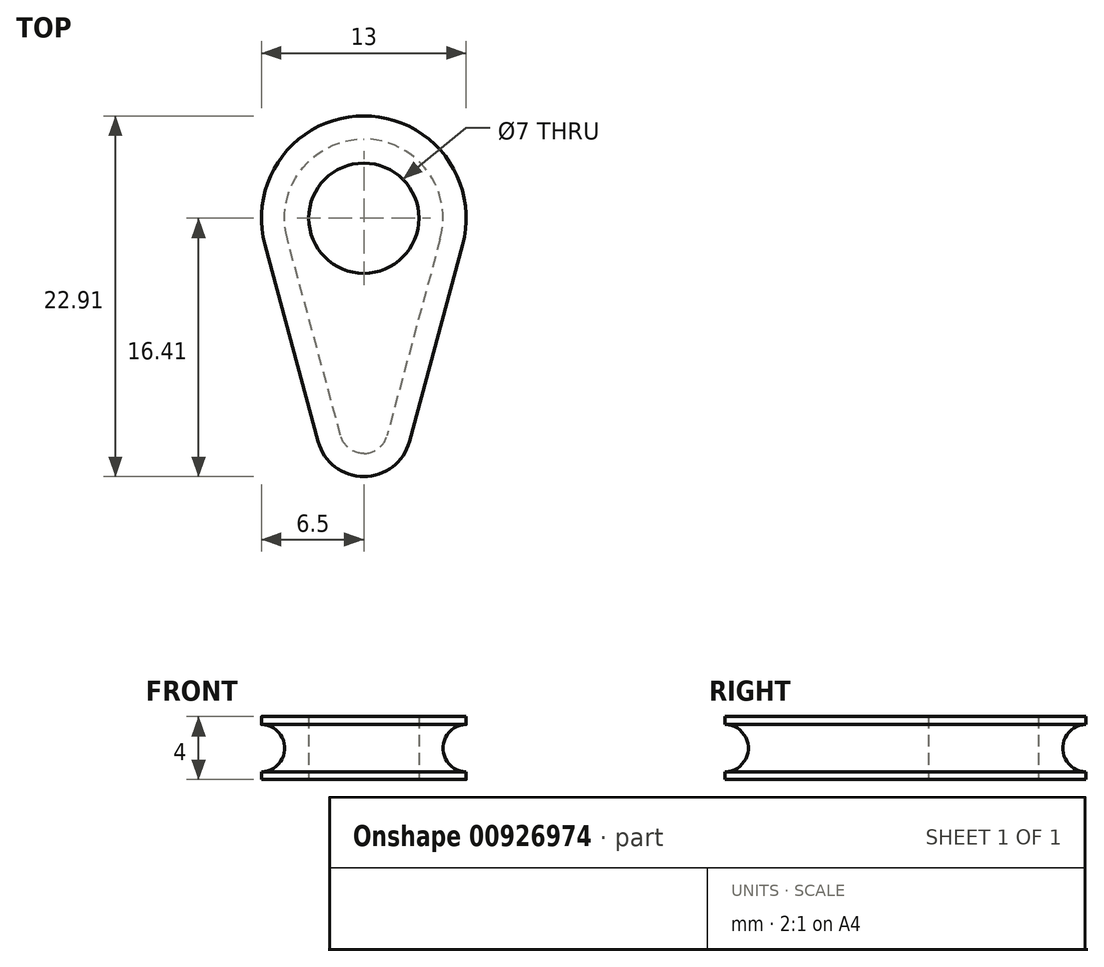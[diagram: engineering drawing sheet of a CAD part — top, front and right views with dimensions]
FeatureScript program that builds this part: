
annotation { "Feature Type Name" : "Feature", "Feature Type Description" : "" }
export const myFeature = defineFeature(function(context is Context, id is Id, definition is map)
    precondition{}
    {
        {
            var Q0;
            Q0=qCreatedBy(makeId("Top.planeOp"),FACE);
            var sketch = newSketch(context, id + "F0", { "sketchPlane" : qUnion([Q0])});
            skLineSegment(sketch, "E0", {"start": v(0, 71.12) * mm, "end": v(0, 6.5) * mm});
            skArc(sketch, "E1", {"start": v(0, 3.5) * mm, "mid": v(-3.5, 0) * mm, "end": v(0, -3.5) * mm});
            skArc(sketch, "E2", {"start": v(0, 6.5) * mm, "mid": v(-5.16, 3.95) * mm, "end": v(-6.27, -1.7) * mm});
            skLineSegment(sketch, "E3", {"start": v(0, 6.5) * mm, "end": v(0, -16.42) * mm});
            skArc(sketch, "E4", {"start": v(-2.9, -14.2) * mm, "mid": v(-1.82, -15.8) * mm, "end": v(0, -16.41) * mm});
            skLineSegment(sketch, "E5", {"start": v(-6.27, -1.7) * mm, "end": v(-2.9, -14.2) * mm});
            skSolve(sketch);
        }
        {
            var Q0;
            {var subQ1=sQuery(id+"F0.wireOp",EDGE,"E2");Q0=makeQuery(id+"F0.imprint","IMPRINT",FACE,{"disambiguationData":[TD([[makeQuery(id+"F0.imprint","IMPRINT",EDGE,{"derivedFrom":subQ1}),1.0]])]});}
            extrude(context, id + "F1", {"entities" : qUnion([Q0]), "depth" : 4 * mm, "offsetDistance" : 25 * mm});
        }
        {
            var Q0;
            Q0=makeQuery(id+"F1.opExtrude","SWEPT_EDGE",EDGE,{"disambiguationData":[OSD([sQuery(id+"F0.wireOp",EDGE,"E4"),sQuery(id+"F0.wireOp",EDGE,"E5")])]});
            cPlane(context, id + "F2", {"entities" : qUnion([Q0]), "cplaneType" : CPlaneType.LINE_ANGLE, "offset" : 25 * mm, "angle" : 75 * degree, "width" : 150 * mm, "height" : 150 * mm});
        }
        {
            var Q0;
            Q0=qCreatedBy(id+"F2.planeOp",FACE);
            var sketch = newSketch(context, id + "F3", { "sketchPlane" : qUnion([Q0])});
            skArc(sketch, "E6", {"start": v(6.5, 3.5) * mm, "mid": v(5, 2) * mm, "end": v(6.5, 0.5) * mm});
            skLineSegment(sketch, "E7", {"start": v(6.5, 3.5) * mm, "end": v(6.5, 0.5) * mm});
            skSolve(sketch);
        }
        {
            var Q0;
            Q0 = qSketchRegion(id + "F3", true);
            var Q1;
            Q1=makeQuery(id+"F1.opExtrude","CAP_EDGE",EDGE,{"disambiguationData":[OSD([sQuery(id+"F0.wireOp",EDGE,"E4")])],"isStart":true});
            var Q2;
            Q2=makeQuery(id+"F1.opExtrude","CAP_EDGE",EDGE,{"disambiguationData":[OSD([sQuery(id+"F0.wireOp",EDGE,"E5")])],"isStart":true});
            var Q3;
            Q3=makeQuery(id+"F1.opExtrude","CAP_EDGE",EDGE,{"disambiguationData":[OSD([sQuery(id+"F0.wireOp",EDGE,"E2")])],"isStart":true});
            sweep(context, id + "F4", {"operationType" : NewBodyOperationType.REMOVE, "profiles" : qUnion([Q0]), "path" : qUnion([Q1, Q2, Q3])});
        }
        {
            var Q0;
            Q0=makeQuery(id+"F1.opExtrude","SWEPT_BODY",BODY,{"disambiguationData":[OSD([sQuery(id+"F0.wireOp",EDGE,"E1"),sQuery(id+"F0.wireOp",EDGE,"E2"),sQuery(id+"F0.wireOp",EDGE,"rY96AKfs-JU4n-LT8b-h3Ca-OXywf6S2JK09"),sQuery(id+"F0.wireOp",EDGE,"f2f6bcbf-8a26-4b1f-9b1e-a9f5522c723e.filletArc"),sQuery(id+"F0.wireOp",EDGE,"E3")])]});
            var Q1;
            Q1=qCreatedBy(makeId("Right.planeOp"),FACE);
            mirror(context, id + "F5", {"operationType" : NewBodyOperationType.ADD, "entities" : qUnion([Q0]), "mirrorPlane" : qUnion([Q1])});
        }
    });
